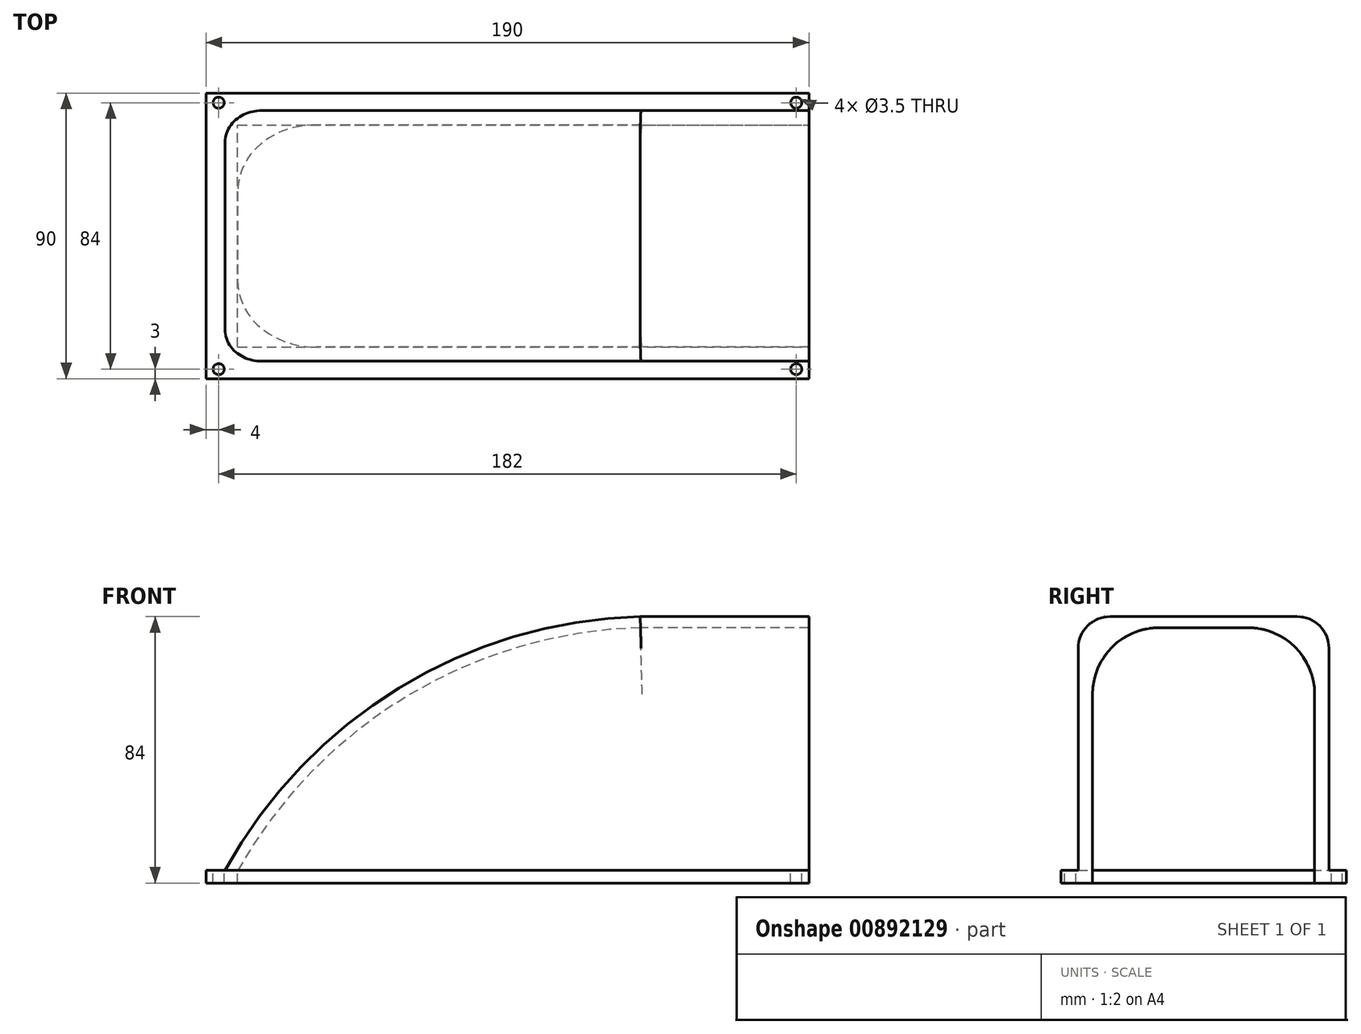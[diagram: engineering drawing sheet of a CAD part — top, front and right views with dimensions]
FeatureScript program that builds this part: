
annotation { "Feature Type Name" : "Feature", "Feature Type Description" : "" }
export const myFeature = defineFeature(function(context is Context, id is Id, definition is map)
    precondition{}
    {
        {
            var Q0;
            Q0=qCreatedBy(makeId("Top.planeOp"),FACE);
            var sketch = newSketch(context, id + "F0", { "sketchPlane" : qUnion([Q0])});
            skLineSegment(sketch, "E0.bottom", {"start": v(-110, -35) * mm, "end": v(110, -35) * mm});
            skLineSegment(sketch, "E0.top", {"start": v(-110, 35) * mm, "end": v(110, 35) * mm});
            skLineSegment(sketch, "E0.left", {"start": v(-110, -35) * mm, "end": v(-110, 35) * mm});
            skLineSegment(sketch, "E0.right", {"start": v(110, -35) * mm, "end": v(110, 35) * mm});
            skPoint(sketch, "E0.middle", {"position": v(0, 0) * mm});
            skLineSegment(sketch, "E1.0", {"start": v(-120, 45) * mm, "end": v(120, 45) * mm});
            skLineSegment(sketch, "E1.1", {"start": v(-120, -45) * mm, "end": v(-120, 45) * mm});
            skLineSegment(sketch, "E1.2", {"start": v(-120, -45) * mm, "end": v(120, -45) * mm});
            skLineSegment(sketch, "E1.3", {"start": v(120, -45) * mm, "end": v(120, 45) * mm});
            skPoint(sketch, "E2", {"position": v(70, -45) * mm});
            skLineSegment(sketch, "E3", {"start": v(70, -45) * mm, "end": v(70, 45) * mm});
            skLineSegment(sketch, "E4.0", {"start": v(-114, 39) * mm, "end": v(110, 39) * mm});
            skLineSegment(sketch, "E4.1", {"start": v(-114, -39) * mm, "end": v(-114, 39) * mm});
            skLineSegment(sketch, "E4.2", {"start": v(-114, -39) * mm, "end": v(110, -39) * mm});
            skPoint(sketch, "E5", {"position": v(-116, 42) * mm});
            skPoint(sketch, "E6", {"position": v(-116, -42) * mm});
            skPoint(sketch, "E7", {"position": v(66, -42) * mm});
            skPoint(sketch, "E8", {"position": v(66, 42) * mm});
            skSolve(sketch);
        }
        {
            var Q0;
            {var subQ5=sQuery(id+"F0.wireOp",EDGE,"E1.1");Q0=makeQuery(id+"F0.imprint","IMPRINT",FACE,{"disambiguationData":[TD([[makeQuery(id+"F0.imprint","IMPRINT",EDGE,{"derivedFrom":subQ5}),-1.0]])]});}
            var Q1;
            {var subQ5=sQuery(id+"F0.wireOp",EDGE,"E0.left");Q1=makeQuery(id+"F0.imprint","IMPRINT",FACE,{"disambiguationData":[TD([[makeQuery(id+"F0.imprint","IMPRINT",EDGE,{"derivedFrom":subQ5}),1.0]])]});}
            extrude(context, id + "F1", {"entities" : qUnion([Q0, Q1]), "oppositeDirection" : true, "depth" : 4 * mm, "offsetDistance" : 25 * mm});
        }
        {
            var Q0;
            Q0=qCreatedBy(makeId("Front.planeOp"),FACE);
            var sketch = newSketch(context, id + "F2", { "sketchPlane" : qUnion([Q0])});
            skPoint(sketch, "E9", {"position": v(-110, 0) * mm});
            skPoint(sketch, "E10", {"position": v(-114, 0) * mm});
            skPoint(sketch, "E11", {"position": v(70, 0) * mm});
            skPoint(sketch, "E12", {"position": v(70, 80) * mm});
            skLineSegment(sketch, "E13", {"start": v(70, 80) * mm, "end": v(16.83, 80) * mm});
            skArc(sketch, "E14", {"start": v(16.83, 80) * mm, "mid": v(-59.24, 57.44) * mm, "end": v(-114, 0) * mm});
            skLineSegment(sketch, "E15", {"start": v(70, 80) * mm, "end": v(70, 0) * mm});
            skArc(sketch, "E16.0", {"start": v(16.88, 76.5) * mm, "mid": v(-56.62, 54.94) * mm, "end": v(-110, 0) * mm});
            skLineSegment(sketch, "E16.1", {"start": v(65, 76.5) * mm, "end": v(16.88, 76.5) * mm});
            skLineSegment(sketch, "E17", {"start": v(-114, 0) * mm, "end": v(70, 0) * mm});
            skLineSegment(sketch, "E18", {"start": v(65, 76.5) * mm, "end": v(70, 76.5) * mm});
            skSolve(sketch);
        }
        {
            var Q0;
            Q0 = qSketchRegion(id + "F2", true);
            extrude(context, id + "F3", {"entities" : qUnion([Q0]), "operationType" : NewBodyOperationType.ADD, "endBound" : BoundingType.SYMMETRIC, "depth" : 79 * mm, "offsetDistance" : 25 * mm});
        }
        {
            var Q0;
            {var subQ3=sQuery(id+"F2.wireOp",EDGE,"E16.0");Q0=makeQuery(id+"F2.imprint","IMPRINT",FACE,{"disambiguationData":[TD([[makeQuery(id+"F2.imprint","IMPRINT",EDGE,{"derivedFrom":subQ3}),1.0]])]});}
            var Q1;
            Q1=makeQuery(id+"F1.opExtrude","SWEPT_FACE",FACE,{"disambiguationData":[OSD([sQuery(id+"F0.wireOp",EDGE,"E0.top")])]});
            extrude(context, id + "F4", {"entities" : qUnion([Q0]), "operationType" : NewBodyOperationType.REMOVE, "endBound" : BoundingType.UP_TO_SURFACE, "oppositeDirection" : true, "depth" : 70 * mm, "endBoundEntityFace" : qUnion([Q1]), "offsetDistance" : 25 * mm});
        }
        {
            var Q0;
            {var subQ3=sQuery(id+"F2.wireOp",EDGE,"E16.0");Q0=makeQuery(id+"F2.imprint","IMPRINT",FACE,{"disambiguationData":[TD([[makeQuery(id+"F2.imprint","IMPRINT",EDGE,{"derivedFrom":subQ3}),1.0]])]});}
            var Q1;
            Q1=makeQuery(id+"F1.opExtrude","SWEPT_FACE",FACE,{"disambiguationData":[OSD([sQuery(id+"F0.wireOp",EDGE,"E0.bottom")])]});
            extrude(context, id + "F5", {"entities" : qUnion([Q0]), "operationType" : NewBodyOperationType.REMOVE, "endBound" : BoundingType.UP_TO_SURFACE, "depth" : 25 * mm, "endBoundEntityFace" : qUnion([Q1]), "offsetDistance" : 25 * mm});
        }
        {
            var Q0;
            Q0=makeQuery(id+"F4.boolean.opBoolean","COPY",EDGE,{"derivedFrom":makeQuery(id+"F4.opExtrude","CAP_EDGE",EDGE,{"disambiguationData":[OSD([sQuery(id+"F2.wireOp",EDGE,"E16.0")])],"isStart":false})});
            var Q1;
            Q1=makeQuery(id+"F5.boolean.opBoolean","COPY",EDGE,{"derivedFrom":makeQuery(id+"F5.opExtrude","CAP_EDGE",EDGE,{"disambiguationData":[OSD([sQuery(id+"F2.wireOp",EDGE,"E16.0")])],"isStart":false})});
            fillet(context, id + "F6", {"entities" : qUnion([Q0, Q1]), "radius" : 21 * mm, "tangentPropagation" : true, "allowEdgeOverflow" : false});
        }
        {
            var Q0;
            Q0=makeQuery(id+"F3.opExtrude","CAP_EDGE",EDGE,{"disambiguationData":[OSD([sQuery(id+"F2.wireOp",EDGE,"E14")])],"isStart":true});
            var Q1;
            Q1=makeQuery(id+"F3.opExtrude","CAP_EDGE",EDGE,{"disambiguationData":[OSD([sQuery(id+"F2.wireOp",EDGE,"E14")])],"isStart":false});
            fillet(context, id + "F7", {"entities" : qUnion([Q0, Q1]), "radius" : 10 * mm, "tangentPropagation" : true, "allowEdgeOverflow" : false});
        }
        {
            var Q0;
            Q0=sQuery(id+"F0.wireOp",VERTEX,"E5");
            var Q1;
            Q1=sQuery(id+"F0.wireOp",VERTEX,"E8");
            var Q2;
            Q2=sQuery(id+"F0.wireOp",VERTEX,"E7");
            var Q3;
            Q3=sQuery(id+"F0.wireOp",VERTEX,"E6");
            var Q4;
            Q4=makeQuery(id+"F1.opExtrude","SWEPT_BODY",BODY,{"disambiguationData":[OSD([sQuery(id+"F0.wireOp",EDGE,"E0.bottom"),sQuery(id+"F0.wireOp",EDGE,"E0.top"),sQuery(id+"F0.wireOp",EDGE,"E0.left"),sQuery(id+"F0.wireOp",EDGE,"E1.0"),sQuery(id+"F0.wireOp",EDGE,"E1.1"),sQuery(id+"F0.wireOp",EDGE,"E1.2"),sQuery(id+"F0.wireOp",EDGE,"E3")])]});
            hole(context, id + "F8", {"style" : HoleStyle.SIMPLE, "endStyle" : HoleEndStyle.THROUGH, "holeDiameter" : 3.5 * mm, "majorDiameter" : 5 * mm, "isTappedThrough" : true, "tappedDepth" : 12 * mm, "tapClearance" : 3, "startFromSketch" : true, "locations" : qUnion([Q0, Q1, Q2, Q3]), "scope" : qUnion([Q4])});
        }
    });
